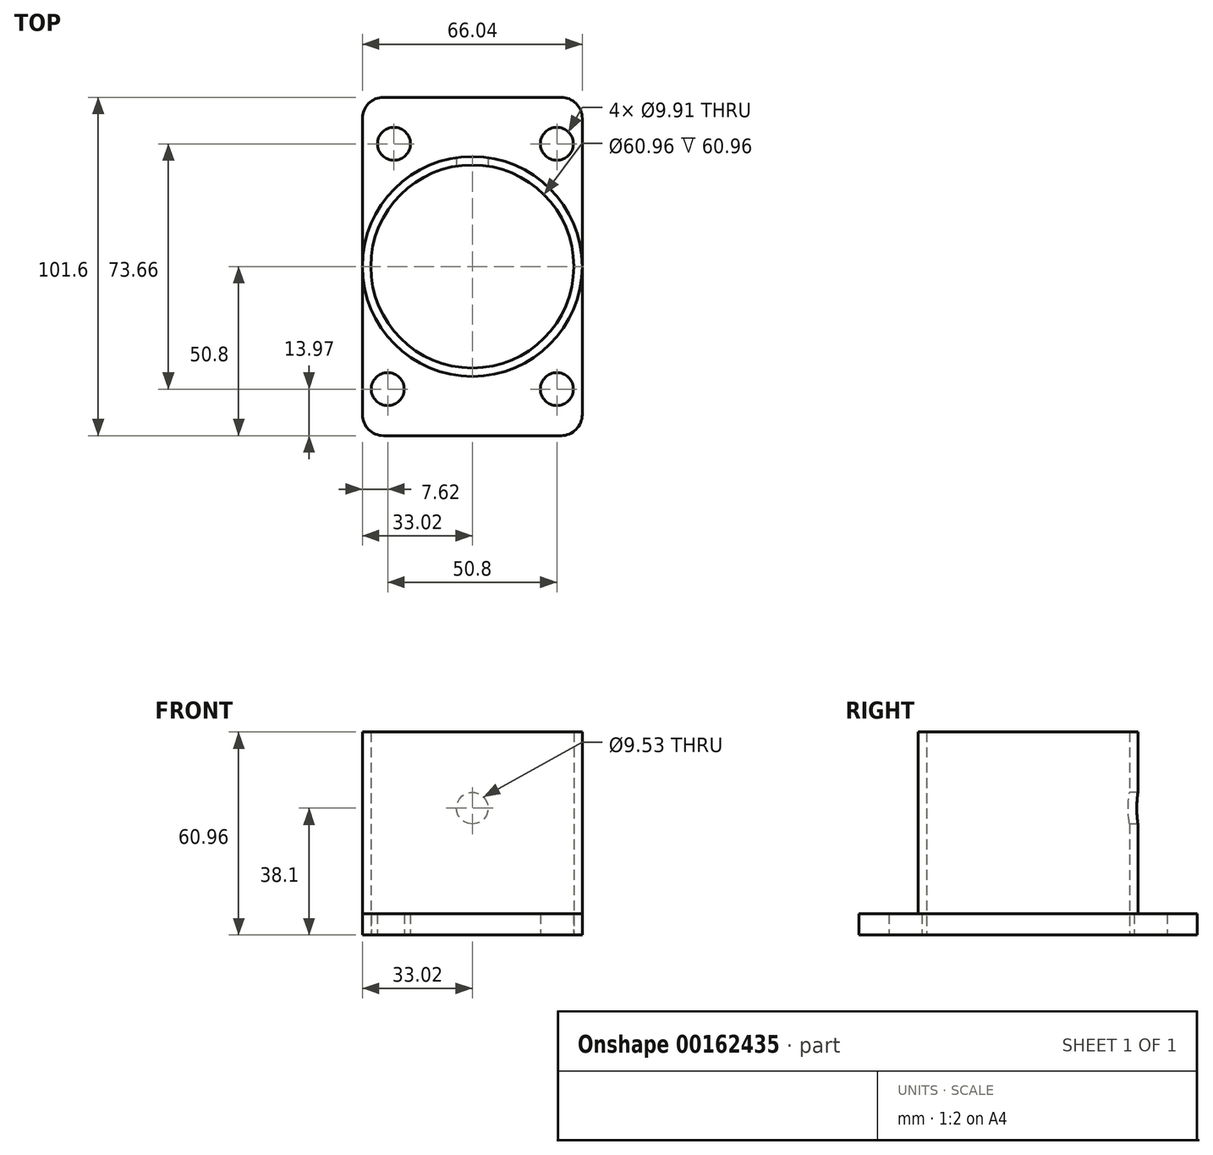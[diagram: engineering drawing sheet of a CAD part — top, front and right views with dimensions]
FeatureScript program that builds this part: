
annotation { "Feature Type Name" : "Feature", "Feature Type Description" : "" }
export const myFeature = defineFeature(function(context is Context, id is Id, definition is map)
    precondition{}
    {
        {
            var Q0;
            Q0=qCreatedBy(makeId("Top.planeOp"),FACE);
            var sketch = newSketch(context, id + "F0", { "sketchPlane" : qUnion([Q0])});
            skCircle(sketch, "E0", {"center": v(0, 0) * mm, "radius": 30.48 * mm});
            skCircle(sketch, "E1", {"center": v(-23.52, 36.83) * mm, "radius": 4.95 * mm});
            skCircle(sketch, "E2", {"center": v(25.4, 36.83) * mm, "radius": 4.95 * mm});
            skCircle(sketch, "E3", {"center": v(25.4, -36.83) * mm, "radius": 4.95 * mm});
            skCircle(sketch, "E4", {"center": v(-25.4, -36.83) * mm, "radius": 4.95 * mm});
            skLineSegment(sketch, "E5.bottom", {"start": v(26.67, 50.8) * mm, "end": v(-26.67, 50.8) * mm});
            skLineSegment(sketch, "E5.top", {"start": v(26.67, -50.8) * mm, "end": v(-26.67, -50.8) * mm});
            skLineSegment(sketch, "E5.left", {"start": v(33.02, 44.45) * mm, "end": v(33.02, -44.45) * mm});
            skLineSegment(sketch, "E5.right", {"start": v(-33.02, 44.45) * mm, "end": v(-33.02, -44.45) * mm});
            skPoint(sketch, "E6.visualSharp", {"position": v(-33.02, 50.8) * mm});
            skArc(sketch, "E6.filletArc", {"start": v(-26.67, 50.8) * mm, "mid": v(-31.16, 48.94) * mm, "end": v(-33.02, 44.45) * mm});
            skPoint(sketch, "E7.visualSharp", {"position": v(33.02, 50.8) * mm});
            skArc(sketch, "E7.filletArc", {"start": v(33.02, 44.45) * mm, "mid": v(31.16, 48.94) * mm, "end": v(26.67, 50.8) * mm});
            skPoint(sketch, "E8.visualSharp", {"position": v(33.02, -50.8) * mm});
            skArc(sketch, "E8.filletArc", {"start": v(26.67, -50.8) * mm, "mid": v(31.16, -48.94) * mm, "end": v(33.02, -44.45) * mm});
            skPoint(sketch, "E9.visualSharp", {"position": v(-33.02, -50.8) * mm});
            skArc(sketch, "E9.filletArc", {"start": v(-33.02, -44.45) * mm, "mid": v(-31.16, -48.94) * mm, "end": v(-26.67, -50.8) * mm});
            skSolve(sketch);
        }
        {
            var Q0;
            Q0 = qSketchRegion(id + "F0", true);
            extrude(context, id + "F1", {"entities" : qUnion([Q0]), "depth" : 6.35 * mm});
        }
        {
            var Q0;
            Q0=makeQuery(id+"F1.opExtrude","CAP_FACE",FACE,{"disambiguationData":[OSD([sQuery(id+"F0.wireOp",EDGE,"E0"),sQuery(id+"F0.wireOp",EDGE,"E1"),sQuery(id+"F0.wireOp",EDGE,"E2"),sQuery(id+"F0.wireOp",EDGE,"E3"),sQuery(id+"F0.wireOp",EDGE,"E4"),sQuery(id+"F0.wireOp",EDGE,"E5.bottom"),sQuery(id+"F0.wireOp",EDGE,"E5.top"),sQuery(id+"F0.wireOp",EDGE,"E5.left"),sQuery(id+"F0.wireOp",EDGE,"E5.right"),sQuery(id+"F0.wireOp",EDGE,"E6.filletArc"),sQuery(id+"F0.wireOp",EDGE,"E7.filletArc"),sQuery(id+"F0.wireOp",EDGE,"E8.filletArc"),sQuery(id+"F0.wireOp",EDGE,"E9.filletArc")])],"isStart":false});
            var sketch = newSketch(context, id + "F2", { "sketchPlane" : qUnion([Q0])});
            skCircle(sketch, "E10", {"center": v(0, 0) * mm, "radius": 33.02 * mm});
            skCircle(sketch, "E11.0", {"center": v(0, 0) * mm, "radius": 30.48 * mm});
            skSolve(sketch);
        }
        {
            var Q0;
            Q0 = qSketchRegion(id + "F2", true);
            extrude(context, id + "F3", {"entities" : qUnion([Q0]), "operationType" : NewBodyOperationType.ADD, "depth" : 54.6 * mm});
        }
        {
            var Q0;
            Q0=qCreatedBy(makeId("Front.planeOp"),FACE);
            var sketch = newSketch(context, id + "F4", { "sketchPlane" : qUnion([Q0])});
            skPoint(sketch, "E12", {"position": v(0, 38.1) * mm});
            skSolve(sketch);
        }
        {
            var Q0;
            Q0=sQuery(id+"F4.wireOp",VERTEX,"E12");
            var Q1;
            Q1=makeQuery(id+"F1.opExtrude","SWEPT_BODY",BODY,{"disambiguationData":[OSD([sQuery(id+"F0.wireOp",EDGE,"E0"),sQuery(id+"F0.wireOp",EDGE,"E1"),sQuery(id+"F0.wireOp",EDGE,"E2"),sQuery(id+"F0.wireOp",EDGE,"E3"),sQuery(id+"F0.wireOp",EDGE,"E4"),sQuery(id+"F0.wireOp",EDGE,"E5.bottom"),sQuery(id+"F0.wireOp",EDGE,"E5.top"),sQuery(id+"F0.wireOp",EDGE,"E5.left"),sQuery(id+"F0.wireOp",EDGE,"E5.right"),sQuery(id+"F0.wireOp",EDGE,"E6.filletArc"),sQuery(id+"F0.wireOp",EDGE,"E7.filletArc"),sQuery(id+"F0.wireOp",EDGE,"E8.filletArc"),sQuery(id+"F0.wireOp",EDGE,"E9.filletArc")])]});
            hole(context, id + "F5", {"style" : HoleStyle.SIMPLE, "endStyle" : HoleEndStyle.THROUGH, "holeDiameter" : 9.52 * mm, "locations" : qUnion([Q0]), "scope" : qUnion([Q1]), "isTappedThrough" : true});
        }
    });
